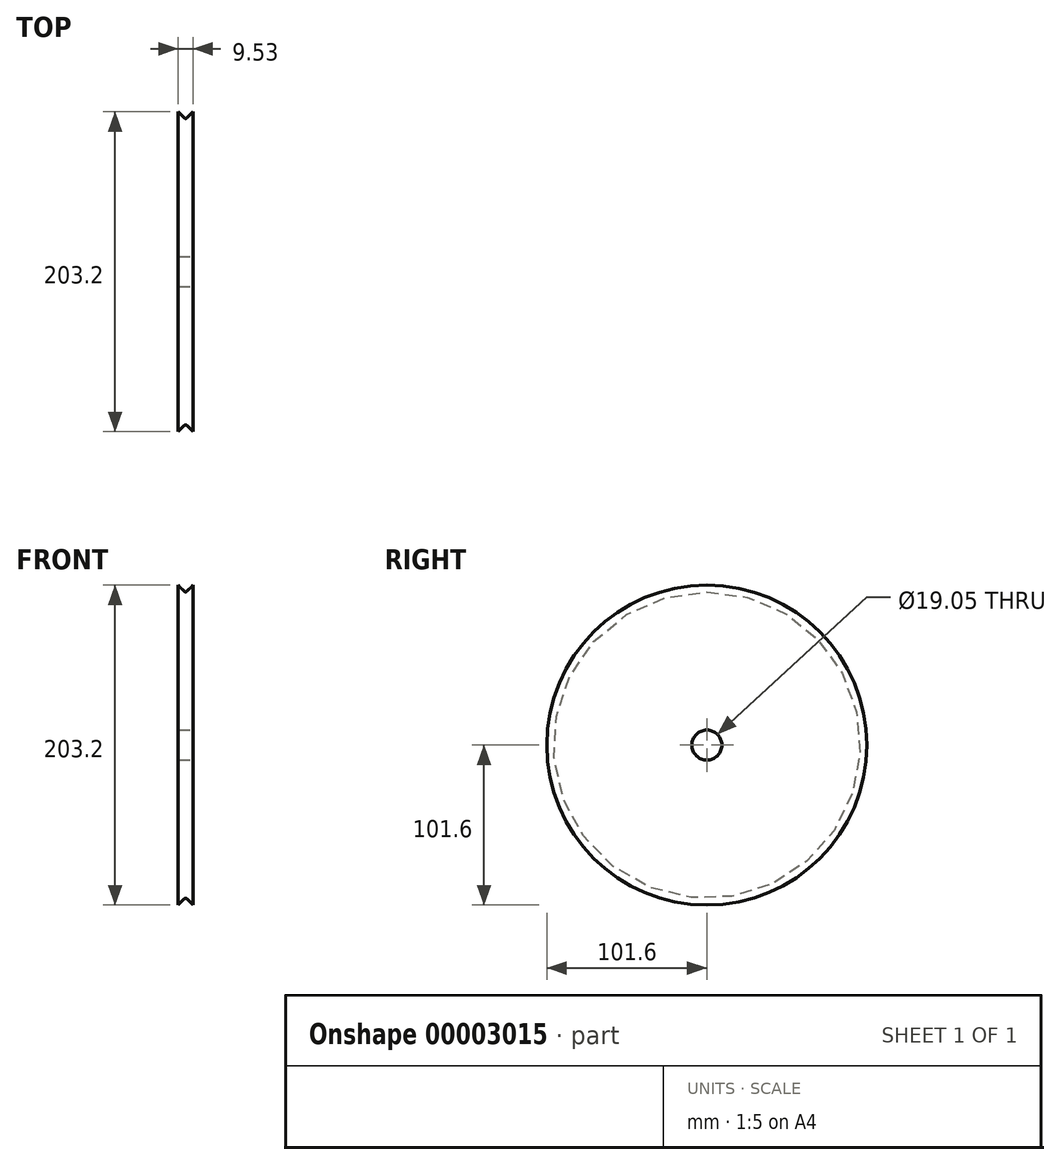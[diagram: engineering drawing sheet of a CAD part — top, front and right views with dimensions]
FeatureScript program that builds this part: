
annotation { "Feature Type Name" : "Feature", "Feature Type Description" : "" }
export const myFeature = defineFeature(function(context is Context, id is Id, definition is map)
    precondition{}
    {
        {
            var Q0;
            Q0=qCreatedBy(makeId("Front.planeOp"),FACE);
            var sketch = newSketch(context, id + "F0", { "sketchPlane" : qUnion([Q0])});
            skLineSegment(sketch, "E0", {"start": v(0, 0) * mm, "end": v(9.53, 0) * mm});
            skLineSegment(sketch, "E1", {"start": v(9.53, 0) * mm, "end": v(9.52, 101.6) * mm});
            skLineSegment(sketch, "E2", {"start": v(9.53, 101.6) * mm, "end": v(5.66, 97.74) * mm});
            skLineSegment(sketch, "E3", {"start": v(3.86, 97.74) * mm, "end": v(0, 101.6) * mm});
            skLineSegment(sketch, "E4", {"start": v(0, 101.6) * mm, "end": v(0, 0) * mm});
            skPoint(sketch, "E5.visualSharp", {"position": v(4.76, 96.84) * mm});
            skArc(sketch, "E5.filletArc", {"start": v(3.86, 97.74) * mm, "mid": v(4.76, 97.36) * mm, "end": v(5.66, 97.74) * mm});
            skSolve(sketch);
        }
        {
            var Q0;
            Q0=makeQuery(id+"F0.imprint","IMPRINT",FACE,{"disambiguationData":[TD([[makeQuery(id+"F0.imprint","IMPRINT",EDGE,{"derivedFrom":sQuery(id+"F0.wireOp",EDGE,"E0")}),1.0]])]});
            var Q1;
            Q1=sQuery(id+"F0.wireOp",EDGE,"E0");
            revolve(context, id + "F1", {"entities" : qUnion([Q0]), "axis" : qUnion([Q1]), "revolveType" : RevolveType.FULL});
        }
        {
            var Q0;
            Q0=makeQuery(id+"F1.opRevolve","SWEPT_FACE",FACE,{"disambiguationData":[OSD([sQuery(id+"F0.wireOp",EDGE,"E1")])]});
            var sketch = newSketch(context, id + "F2", { "sketchPlane" : qUnion([Q0])});
            skCircle(sketch, "E6", {"center": v(0, 0) * mm, "radius": 9.53 * mm});
            skSolve(sketch);
        }
        {
            var Q0;
            Q0=makeQuery(id+"F2.imprint","IMPRINT",FACE,{"disambiguationData":[TD([[makeQuery(id+"F2.imprint","IMPRINT",EDGE,{"derivedFrom":sQuery(id+"F2.wireOp",EDGE,"E6")}),1.0]])]});
            extrude(context, id + "F3", {"entities" : qUnion([Q0]), "operationType" : NewBodyOperationType.REMOVE, "oppositeDirection" : true, "depth" : 25.4 * mm});
        }
    });
